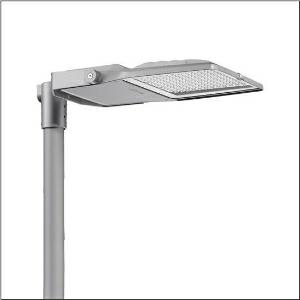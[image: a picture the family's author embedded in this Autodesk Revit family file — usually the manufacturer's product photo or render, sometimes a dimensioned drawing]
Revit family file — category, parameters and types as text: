
# Revit family: floodlight_fl_21_midi___pl61_5xa7786f4c3a_8fd3
name_source: partatom
category: Lighting Fixtures
units: mm (PartAtom-declared; Revit-internal decimal feet)

## family parameters
Cut with Voids When Loaded = No
Host = Face
Light Source = No
Part Type = Normal
Room Calculation Point = No
Round Connector Dimension = Use Diameter
Shared = No

## types (1)
- --- (1 x LED, 36640 lm, 271.6 W, 4000K)
    Apparent Load = 272 VA
    CIE Flux Codes = 33 65 98 100 100
    Color Rendering = 70
    Color Temperature = 4000K
    Default Elevation = 1800 mm
    Description = Floodlight FL 21 midi, floodlight, primary light control with lens, of PMMA, primary optical cover: protective disc, of toughened safety glass, transparent, light distribution: PL61, light emission: direct distribution, installation type: surface-mounted, LED, High Power LED, rated luminous flux: 36.640lm, luminous efficacy: 135lm/W, light colour: 740, colour temperature: 4000K, control gear: Smart Interface (Zhaga)D4i, control: overheat protection, constant luminous flux control, time-dependent luminous flux control, flexible luminous flux parameterisation, pre-setting: logarithmic dimming characteristic, with terminal, 6-pole, mains connection: 220..240V, AC, 50/60Hz, start of lifetime: 272W, end of service life: 287W, reduction: 123W, mast bracket, of diecast aluminium, powder-coated, Siteco® metallic grey (DB 702S), corrosivity category C5 mid according to DIN EN ISO 12944, suitable for swimming pools, chlorine-resistant, sealing non-destructively replaceable, mast bracket, of steel, galvanised, powder-coated, Siteco® metallic grey (DB 702S), Smart Interface below and above, protection rating (complete): IP66, insulation class (complete): insulation class II (safety insulation), certification: CE, ENEC, VDE, protection symbol: D, impact resistance: IK08, permissible operating ambient temperature: -40..+40°C, permissible operating ambient temperature for outdoor applications: -40..+50°C, standard: DIN EN 12944, LABS conformity tested according to VDMA 24364:2018-05, packaging unit: 1 piece

Light Distribution: PL61
    Height = 76 mm
    Lamp = 1 x LED
    Lamp Light Flux = 36640 lm
    Lamp Power = 271.6 W
    Lamp count = 1
    Length = 657 mm
    Luminous efficacy = 135 lm/W
    Manufacturer = Siteco
    ModVariant = No
    Model = 5XA7786F4C3A
    Number of Poles = 1
    OnlyDefault = Yes
    Power Factor = 1
    Product Name = Floodlight FL 21 midi | PL61
    Product group = floodlight | pylon annexe
    ProductGroupID = 6200
    Protection Class = Protection class II
    Protection Degree = IP 66
    RLX_Detail_Level = 1
    RLX_Emergency_Light_Flux = 0 lm
    RLX_Emergency_Type = 0
    RLX_Emergency_Type_DB = No
    RlxData = <blob elided: 104597 chars, md5=84e849d1>
    Socket = socket
    Standby Power = 0 W
    System Light Flux = 36640 lm
    System Power = 272 W
    Type Comments = factory setting: luminous flux: 100 % | dim-lin: 254 | 620 mA
    Type Image = l_1007123.jpg
    URL = http://relux.com
    VarID = @adj_090394
    Voltage = 0 V
    Weight = 0.00 kg
    Width = 442 mm

## geometry (parser evidence)
native form markers: Blend x4, Sweep x13
no freeform markers — native parametric forms only
